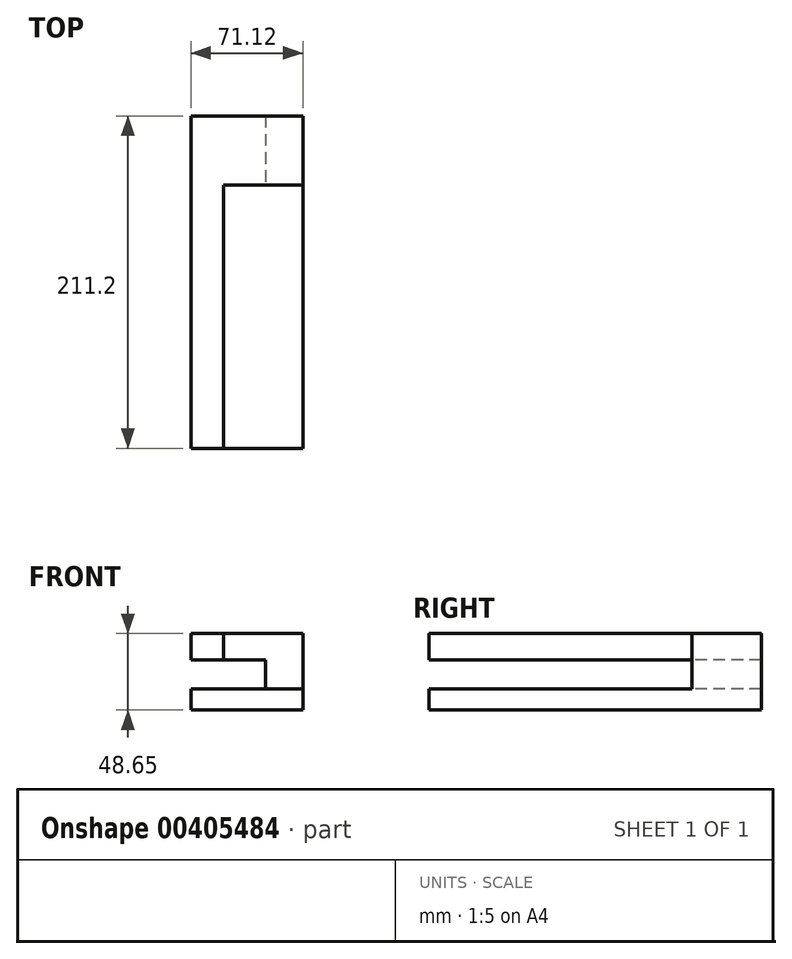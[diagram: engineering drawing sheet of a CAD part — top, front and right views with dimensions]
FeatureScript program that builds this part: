
annotation { "Feature Type Name" : "Feature", "Feature Type Description" : "" }
export const myFeature = defineFeature(function(context is Context, id is Id, definition is map)
    precondition{}
    {
        {
            var Q0;
            Q0=qCreatedBy(makeId("Front.planeOp"),FACE);
            var sketch = newSketch(context, id + "F0", { "sketchPlane" : qUnion([Q0])});
            skLineSegment(sketch, "E0.bottom", {"start": v(-29.88, 23.46) * mm, "end": v(41.24, 23.46) * mm});
            skLineSegment(sketch, "E0.top", {"start": v(-29.88, -25.19) * mm, "end": v(41.24, -25.19) * mm});
            skLineSegment(sketch, "E0.left", {"start": v(-29.88, 23.46) * mm, "end": v(-29.88, -25.19) * mm});
            skLineSegment(sketch, "E0.right", {"start": v(41.24, 23.46) * mm, "end": v(41.24, -25.19) * mm});
            skLineSegment(sketch, "E1", {"start": v(-29.88, -11.9) * mm, "end": v(41.24, -11.9) * mm});
            skLineSegment(sketch, "E2", {"start": v(-29.88, 6.54) * mm, "end": v(41.24, 6.54) * mm});
            skLineSegment(sketch, "E3", {"start": v(-9.1, 23.46) * mm, "end": v(-9.1, 6.54) * mm});
            skLineSegment(sketch, "E4", {"start": v(-9.1, 6.54) * mm, "end": v(17.46, 6.54) * mm});
            skLineSegment(sketch, "E5", {"start": v(17.46, 6.54) * mm, "end": v(17.46, -11.9) * mm});
            skLineSegment(sketch, "E6", {"start": v(17.46, -11.9) * mm, "end": v(41.24, -11.9) * mm});
            skSolve(sketch);
        }
        {
            var Q0;
            {var subQ3=sQuery(id+"F0.wireOp",EDGE,"E3");Q0=makeQuery(id+"F0.imprint","IMPRINT",FACE,{"disambiguationData":[TD([[makeQuery(id+"F0.imprint","IMPRINT",EDGE,{"derivedFrom":subQ3}),-1.0]])]});}
            var Q1;
            {var subQ4=sQuery(id+"F0.wireOp",EDGE,"E1");Q1=makeQuery(id+"F0.imprint","IMPRINT",FACE,{"disambiguationData":[TD([[makeQuery(id+"F0.imprint","IMPRINT",EDGE,{"derivedFrom":subQ4}),1.0]])]});}
            var Q2;
            {var subQ2=sQuery(id+"F0.wireOp",EDGE,"E0.top");Q2=makeQuery(id+"F0.imprint","IMPRINT",FACE,{"disambiguationData":[TD([[makeQuery(id+"F0.imprint","IMPRINT",EDGE,{"derivedFrom":subQ2}),1.0]])]});}
            var Q3;
            {var subQ0=sQuery(id+"F0.wireOp",EDGE,"E3");Q3=makeQuery(id+"F0.imprint","IMPRINT",FACE,{"disambiguationData":[TD([[makeQuery(id+"F0.imprint","IMPRINT",EDGE,{"derivedFrom":subQ0}),1.0]])]});}
            var Q4;
            {var subQ4=sQuery(id+"F0.wireOp",EDGE,"E5");Q4=makeQuery(id+"F0.imprint","IMPRINT",FACE,{"disambiguationData":[TD([[makeQuery(id+"F0.imprint","IMPRINT",EDGE,{"derivedFrom":subQ4}),1.0]])]});}
            extrude(context, id + "F1", {"entities" : qUnion([Q0, Q1, Q2, Q3, Q4]), "oppositeDirection" : true, "depth" : 211.2 * mm});
        }
        {
            var Q0;
            {var subQ0=sQuery(id+"F0.wireOp",EDGE,"E3");Q0=makeQuery(id+"F0.imprint","IMPRINT",FACE,{"disambiguationData":[TD([[makeQuery(id+"F0.imprint","IMPRINT",EDGE,{"derivedFrom":subQ0}),1.0]])]});}
            var Q1;
            {var subQ4=sQuery(id+"F0.wireOp",EDGE,"E5");Q1=makeQuery(id+"F0.imprint","IMPRINT",FACE,{"disambiguationData":[TD([[makeQuery(id+"F0.imprint","IMPRINT",EDGE,{"derivedFrom":subQ4}),1.0]])]});}
            extrude(context, id + "F2", {"entities" : qUnion([Q0, Q1]), "operationType" : NewBodyOperationType.REMOVE, "oppositeDirection" : true, "depth" : 167.2 * mm});
        }
    });
